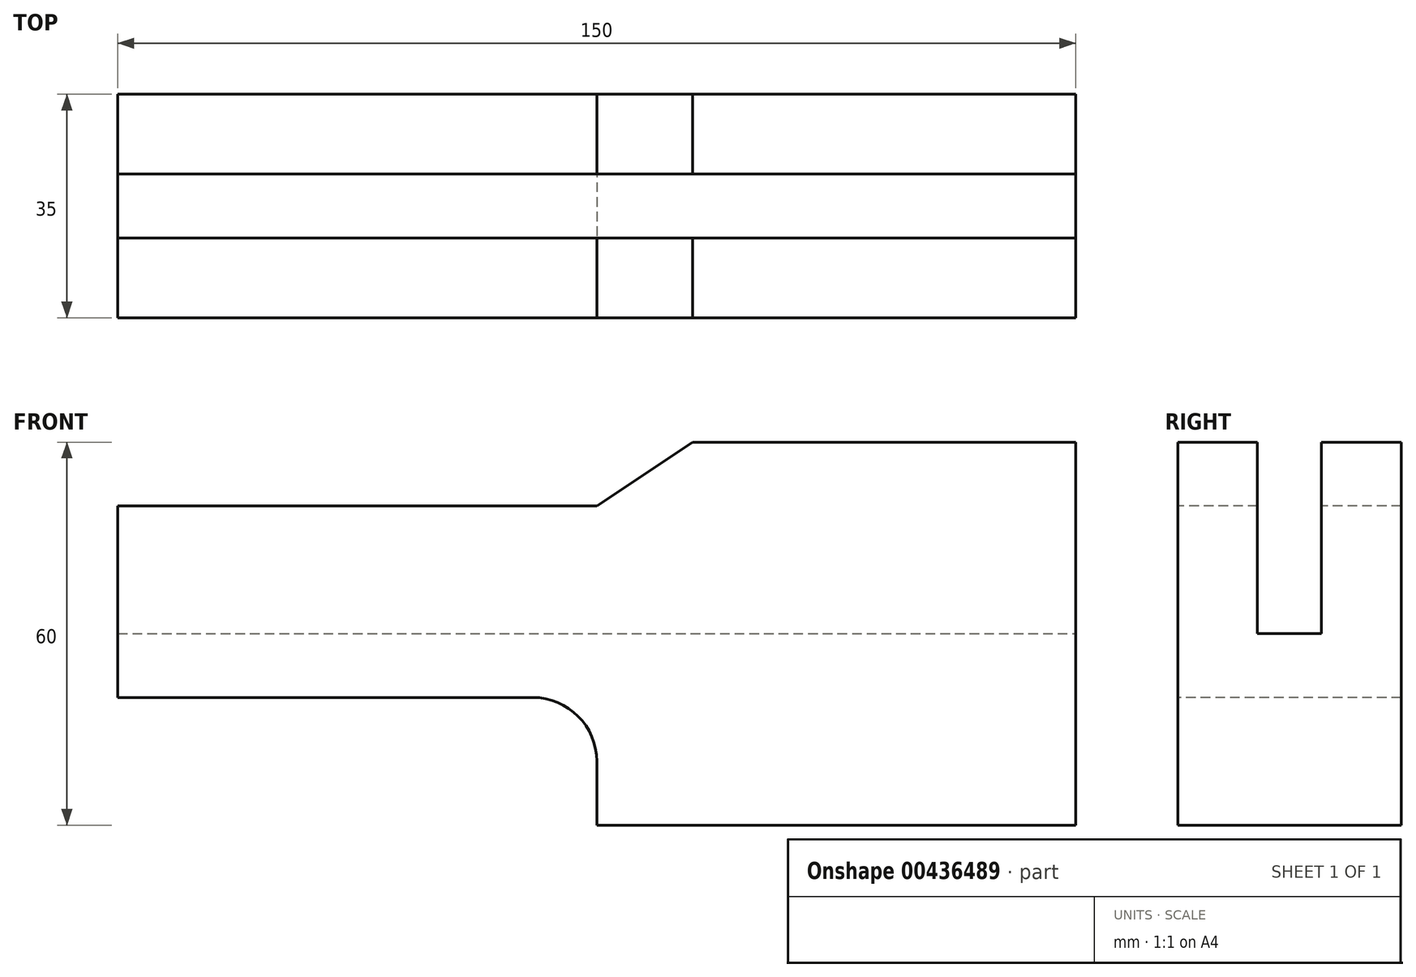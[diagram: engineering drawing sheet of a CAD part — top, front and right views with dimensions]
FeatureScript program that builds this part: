
annotation { "Feature Type Name" : "Feature", "Feature Type Description" : "" }
export const myFeature = defineFeature(function(context is Context, id is Id, definition is map)
    precondition{}
    {
        {
            var Q0;
            Q0=qCreatedBy(makeId("Top.planeOp"),FACE);
            var sketch = newSketch(context, id + "F0", { "sketchPlane" : qUnion([Q0])});
            skLineSegment(sketch, "E0.bottom", {"start": v(-75, 17.5) * mm, "end": v(75, 17.5) * mm});
            skLineSegment(sketch, "E0.top", {"start": v(-75, -17.5) * mm, "end": v(75, -17.5) * mm});
            skLineSegment(sketch, "E0.left", {"start": v(-75, 17.5) * mm, "end": v(-75, -17.5) * mm});
            skLineSegment(sketch, "E0.right", {"start": v(75, 17.5) * mm, "end": v(75, -17.5) * mm});
            skPoint(sketch, "E0.middle", {"position": v(0, 0) * mm});
            skSolve(sketch);
        }
        {
            var Q0;
            Q0 = qSketchRegion(id + "F0", true);
            extrude(context, id + "F1", {"entities" : qUnion([Q0]), "depth" : 60 * mm, "offsetDistance" : 25.4 * mm});
        }
        {
            var Q0;
            Q0=makeQuery(id+"F1.opExtrude","SWEPT_FACE",FACE,{"disambiguationData":[OSD([sQuery(id+"F0.wireOp",EDGE,"E0.right")])]});
            var sketch = newSketch(context, id + "F2", { "sketchPlane" : qUnion([Q0])});
            skLineSegment(sketch, "E1.bottom", {"start": v(-5, 60) * mm, "end": v(5, 60) * mm});
            skLineSegment(sketch, "E1.top", {"start": v(-5, 30) * mm, "end": v(5, 30) * mm});
            skLineSegment(sketch, "E1.left", {"start": v(-5, 60) * mm, "end": v(-5, 30) * mm});
            skLineSegment(sketch, "E1.right", {"start": v(5, 60) * mm, "end": v(5, 30) * mm});
            skSolve(sketch);
        }
        {
            var Q0;
            Q0=makeQuery(id+"F2.imprint","IMPRINT",FACE,{"disambiguationData":[TD([[makeQuery(id+"F2.imprint","IMPRINT",EDGE,{"derivedFrom":sQuery(id+"F2.wireOp",EDGE,"E1.bottom")}),1.0]])]});
            extrude(context, id + "F3", {"entities" : qUnion([Q0]), "operationType" : NewBodyOperationType.REMOVE, "oppositeDirection" : true, "depth" : 150 * mm, "offsetDistance" : 25 * mm});
        }
        {
            var Q0;
            Q0=makeQuery(id+"F1.opExtrude","SWEPT_FACE",FACE,{"disambiguationData":[OSD([sQuery(id+"F0.wireOp",EDGE,"E0.top")])]});
            var sketch = newSketch(context, id + "F4", { "sketchPlane" : qUnion([Q0])});
            skLineSegment(sketch, "E2.bottom", {"start": v(-75, 0) * mm, "end": v(0, 0) * mm});
            skLineSegment(sketch, "E2.top", {"start": v(-75, 20) * mm, "end": v(0, 20) * mm});
            skLineSegment(sketch, "E2.left", {"start": v(-75, 0) * mm, "end": v(-75, 20) * mm});
            skLineSegment(sketch, "E2.right", {"start": v(0, 0) * mm, "end": v(0, 20) * mm});
            skSolve(sketch);
        }
        {
            var Q0;
            Q0 = qSketchRegion(id + "F4", true);
            extrude(context, id + "F5", {"entities" : qUnion([Q0]), "operationType" : NewBodyOperationType.REMOVE, "endBound" : BoundingType.THROUGH_ALL, "oppositeDirection" : true, "depth" : 25 * mm, "offsetDistance" : 25 * mm});
        }
        {
            var Q0;
            Q0=makeQuery(id+"F5.boolean.opBoolean","COPY",EDGE,{"derivedFrom":makeQuery(id+"F5.opExtrude","SWEPT_EDGE",EDGE,{"disambiguationData":[OSD([sQuery(id+"F4.wireOp",EDGE,"E2.top"),sQuery(id+"F4.wireOp",EDGE,"E2.right")])]})});
            fillet(context, id + "F6", {"entities" : qUnion([Q0]), "tangentPropagation" : true, "radius" : 10 * mm, "defaultsChanged" : true, "vertexSettings" : [], "allowEdgeOverflow" : false});
        }
        {
            var Q0;
            Q0=makeQuery(id+"F1.opExtrude","SWEPT_FACE",FACE,{"disambiguationData":[OSD([sQuery(id+"F0.wireOp",EDGE,"E0.top")])]});
            var sketch = newSketch(context, id + "F7", { "sketchPlane" : qUnion([Q0])});
            skLineSegment(sketch, "E3.bottom", {"start": v(-75, 60) * mm, "end": v(15, 60) * mm});
            skLineSegment(sketch, "E3.top", {"start": v(-75, 50) * mm, "end": v(0, 50) * mm});
            skLineSegment(sketch, "E3.left", {"start": v(-75, 60) * mm, "end": v(-75, 50) * mm});
            skLineSegment(sketch, "E4", {"start": v(15, 60) * mm, "end": v(0, 50) * mm});
            skSolve(sketch);
        }
        {
            var Q0;
            Q0 = qSketchRegion(id + "F7", true);
            extrude(context, id + "F8", {"entities" : qUnion([Q0]), "operationType" : NewBodyOperationType.REMOVE, "endBound" : BoundingType.THROUGH_ALL, "oppositeDirection" : true, "depth" : 25 * mm, "offsetDistance" : 25 * mm});
        }
    });
